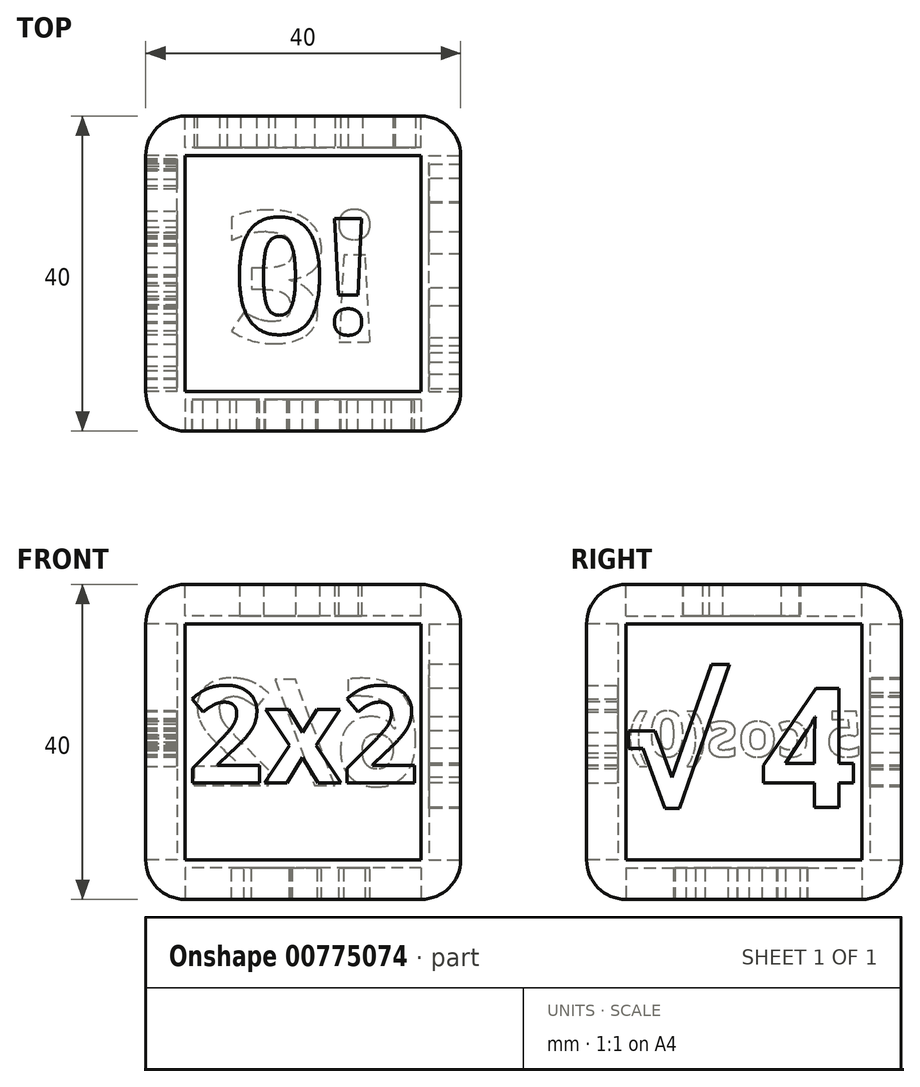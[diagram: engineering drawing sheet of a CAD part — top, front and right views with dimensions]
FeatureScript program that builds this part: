
annotation { "Feature Type Name" : "Feature", "Feature Type Description" : "" }
export const myFeature = defineFeature(function(context is Context, id is Id, definition is map)
    precondition{}
    {
        {
            var Q0;
            Q0=qCreatedBy(makeId("Top.planeOp"),FACE);
            var sketch = newSketch(context, id + "F0", { "sketchPlane" : qUnion([Q0])});
            skLineSegment(sketch, "E0.bottom", {"start": v(20, -20) * mm, "end": v(-20, -20) * mm});
            skLineSegment(sketch, "E0.top", {"start": v(20, 20) * mm, "end": v(-20, 20) * mm});
            skLineSegment(sketch, "E0.left", {"start": v(20, -20) * mm, "end": v(20, 20) * mm});
            skLineSegment(sketch, "E0.right", {"start": v(-20, -20) * mm, "end": v(-20, 20) * mm});
            skPoint(sketch, "E0.middle", {"position": v(0, 0) * mm});
            skSolve(sketch);
        }
        {
            var Q0;
            Q0=makeQuery(id+"F0.imprint","IMPRINT",FACE,{"disambiguationData":[TD([[makeQuery(id+"F0.imprint","IMPRINT",EDGE,{"derivedFrom":sQuery(id+"F0.wireOp",EDGE,"E0.bottom")}),-1.0]])]});
            extrude(context, id + "F1", {"entities" : qUnion([Q0]), "depth" : 40 * mm, "offsetDistance" : 25 * mm});
        }
        {
            var Q0;
            Q0=makeQuery(id+"F1.opExtrude","CAP_FACE",FACE,{"disambiguationData":[OSD([sQuery(id+"F0.wireOp",EDGE,"E0.bottom"),sQuery(id+"F0.wireOp",EDGE,"E0.top"),sQuery(id+"F0.wireOp",EDGE,"E0.left"),sQuery(id+"F0.wireOp",EDGE,"E0.right")])],"isStart":false});
            var Q1;
            Q1=makeQuery(id+"F1.opExtrude","CAP_FACE",FACE,{"disambiguationData":[OSD([sQuery(id+"F0.wireOp",EDGE,"E0.bottom"),sQuery(id+"F0.wireOp",EDGE,"E0.top"),sQuery(id+"F0.wireOp",EDGE,"E0.left"),sQuery(id+"F0.wireOp",EDGE,"E0.right")])],"isStart":true});
            var Q2;
            Q2=makeQuery(id+"F1.opExtrude","SWEPT_FACE",FACE,{"disambiguationData":[OSD([sQuery(id+"F0.wireOp",EDGE,"E0.bottom")])]});
            var Q3;
            Q3=makeQuery(id+"F1.opExtrude","SWEPT_FACE",FACE,{"disambiguationData":[OSD([sQuery(id+"F0.wireOp",EDGE,"E0.top")])]});
            fillet(context, id + "F2", {"entities" : qUnion([Q0, Q1, Q2, Q3]), "radius" : 5 * mm, "tangentPropagation" : true, "allowEdgeOverflow" : false});
        }
        {
            var Q0;
            Q0=makeQuery(id+"F1.opExtrude","CAP_FACE",FACE,{"disambiguationData":[OSD([sQuery(id+"F0.wireOp",EDGE,"E0.bottom"),sQuery(id+"F0.wireOp",EDGE,"E0.top"),sQuery(id+"F0.wireOp",EDGE,"E0.left"),sQuery(id+"F0.wireOp",EDGE,"E0.right")])],"isStart":false});
            extrude(context, id + "F3", {"entities" : qUnion([Q0]), "operationType" : NewBodyOperationType.REMOVE, "oppositeDirection" : true, "depth" : 4 * mm, "offsetDistance" : 25 * mm});
        }
        {
            var Q0;
            Q0=makeQuery(id+"F1.opExtrude","SWEPT_FACE",FACE,{"disambiguationData":[OSD([sQuery(id+"F0.wireOp",EDGE,"E0.top")])]});
            extrude(context, id + "F4", {"entities" : qUnion([Q0]), "operationType" : NewBodyOperationType.REMOVE, "oppositeDirection" : true, "depth" : 4 * mm, "offsetDistance" : 25 * mm});
        }
        {
            var Q0;
            Q0=makeQuery(id+"F1.opExtrude","SWEPT_FACE",FACE,{"disambiguationData":[OSD([sQuery(id+"F0.wireOp",EDGE,"E0.left")])]});
            extrude(context, id + "F5", {"entities" : qUnion([Q0]), "operationType" : NewBodyOperationType.REMOVE, "oppositeDirection" : true, "depth" : 4 * mm, "offsetDistance" : 25 * mm});
        }
        {
            var Q0;
            Q0=makeQuery(id+"F1.opExtrude","SWEPT_FACE",FACE,{"disambiguationData":[OSD([sQuery(id+"F0.wireOp",EDGE,"E0.bottom")])]});
            extrude(context, id + "F6", {"entities" : qUnion([Q0]), "operationType" : NewBodyOperationType.REMOVE, "oppositeDirection" : true, "depth" : 4 * mm, "offsetDistance" : 25 * mm});
        }
        {
            var Q0;
            Q0=makeQuery(id+"F1.opExtrude","SWEPT_FACE",FACE,{"disambiguationData":[OSD([sQuery(id+"F0.wireOp",EDGE,"E0.right")])]});
            extrude(context, id + "F7", {"entities" : qUnion([Q0]), "operationType" : NewBodyOperationType.REMOVE, "oppositeDirection" : true, "depth" : 4 * mm, "offsetDistance" : 25 * mm});
        }
        {
            var Q0;
            Q0=makeQuery(id+"F1.opExtrude","CAP_FACE",FACE,{"disambiguationData":[OSD([sQuery(id+"F0.wireOp",EDGE,"E0.bottom"),sQuery(id+"F0.wireOp",EDGE,"E0.top"),sQuery(id+"F0.wireOp",EDGE,"E0.left"),sQuery(id+"F0.wireOp",EDGE,"E0.right")])],"isStart":true});
            extrude(context, id + "F8", {"entities" : qUnion([Q0]), "operationType" : NewBodyOperationType.REMOVE, "oppositeDirection" : true, "depth" : 4 * mm, "offsetDistance" : 25 * mm});
        }
        {
            var Q0;
            Q0=makeQuery(id+"F3.boolean.opBoolean","COPY",FACE,{"derivedFrom":makeQuery(id+"F3.opExtrude","CAP_FACE",FACE,{"disambiguationData":[OSD([sQuery(id+"F0.wireOp",EDGE,"E0.bottom"),sQuery(id+"F0.wireOp",EDGE,"E0.top"),sQuery(id+"F0.wireOp",EDGE,"E0.left"),sQuery(id+"F0.wireOp",EDGE,"E0.right")])],"isStart":false})});
            var sketch = newSketch(context, id + "F9", { "sketchPlane" : qUnion([Q0])});
            skText(sketch, "E1", { "text": "0!", "fontName": "OpenSans-Bold.ttf"});
            const initialGuessF9  = {"E1": [-0.00883, -0.00758, 1, 0, 0.01467]};
            skSetInitialGuess(sketch, initialGuessF9);
            skSolve(sketch);
        }
        {
            var Q0;
            Q0=makeQuery(id+"F9.imprint","IMPRINT",FACE,{"disambiguationData":[TD([[makeQuery(id+"F9.imprint","IMPRINT",EDGE,{"derivedFrom":sQuery(id+"F9.wireOp",EDGE,"E1.sketch_text.stroke-20")}),-1.0]])]});
            var Q1;
            Q1=makeQuery(id+"F9.imprint","IMPRINT",FACE,{"disambiguationData":[TD([[makeQuery(id+"F9.imprint","IMPRINT",EDGE,{"derivedFrom":sQuery(id+"F9.wireOp",EDGE,"E1.sketch_text.stroke-16")}),-1.0]])]});
            var Q2;
            Q2=makeQuery(id+"F9.imprint","IMPRINT",FACE,{"disambiguationData":[TD([[makeQuery(id+"F9.imprint","IMPRINT",EDGE,{"derivedFrom":sQuery(id+"F9.wireOp",EDGE,"E1.sketch_text.stroke-0")}),-1.0]])]});
            extrude(context, id + "F10", {"entities" : qUnion([Q0, Q1, Q2]), "operationType" : NewBodyOperationType.ADD, "depth" : 4 * mm, "offsetDistance" : 25 * mm});
        }
        {
            var Q0;
            Q0=makeQuery(id+"F5.boolean.opBoolean","COPY",FACE,{"derivedFrom":makeQuery(id+"F5.opExtrude","CAP_FACE",FACE,{"disambiguationData":[OSD([sQuery(id+"F0.wireOp",EDGE,"E0.left")])],"isStart":false})});
            var sketch = newSketch(context, id + "F11", { "sketchPlane" : qUnion([Q0])});
            skText(sketch, "E2", { "text": "√ 4", "fontName": "OpenSans-Bold.ttf"});
            const initialGuessF11  = {"E2": [-0.01505, 0.01168, 1, 0, 0.01527]};
            skSetInitialGuess(sketch, initialGuessF11);
            skSolve(sketch);
        }
        {
            var Q0;
            Q0=makeQuery(id+"F11.imprint","IMPRINT",FACE,{"disambiguationData":[TD([[makeQuery(id+"F11.imprint","IMPRINT",EDGE,{"derivedFrom":sQuery(id+"F11.wireOp",EDGE,"E2.sketch_text.stroke-0")}),-1.0]])]});
            var Q1;
            Q1=makeQuery(id+"F11.imprint","IMPRINT",FACE,{"disambiguationData":[TD([[makeQuery(id+"F11.imprint","IMPRINT",EDGE,{"derivedFrom":sQuery(id+"F11.wireOp",EDGE,"E2.sketch_text.stroke-9")}),-1.0]])]});
            extrude(context, id + "F12", {"entities" : qUnion([Q0, Q1]), "operationType" : NewBodyOperationType.ADD, "depth" : 4 * mm, "offsetDistance" : 25 * mm});
        }
        {
            var Q0;
            Q0=makeQuery(id+"F4.boolean.opBoolean","COPY",FACE,{"derivedFrom":makeQuery(id+"F4.opExtrude","CAP_FACE",FACE,{"disambiguationData":[OSD([sQuery(id+"F0.wireOp",EDGE,"E0.top")])],"isStart":false})});
            var sketch = newSketch(context, id + "F13", { "sketchPlane" : qUnion([Q0])});
            skText(sketch, "E3", { "text": "6/2\n", "fontName": "OpenSans-Bold.ttf"});
            const initialGuessF13  = {"E3": [-0.01494, 0.01446, 1, 0, 0.0136]};
            skSetInitialGuess(sketch, initialGuessF13);
            skSolve(sketch);
        }
        {
            var Q0;
            Q0 = qSketchRegion(id + "F13", true);
            extrude(context, id + "F14", {"entities" : qUnion([Q0]), "operationType" : NewBodyOperationType.ADD, "depth" : 4 * mm, "offsetDistance" : 25 * mm});
        }
        {
            var Q0;
            Q0=makeQuery(id+"F6.boolean.opBoolean","COPY",FACE,{"derivedFrom":makeQuery(id+"F6.opExtrude","CAP_FACE",FACE,{"disambiguationData":[OSD([sQuery(id+"F0.wireOp",EDGE,"E0.bottom")])],"isStart":false})});
            var sketch = newSketch(context, id + "F15", { "sketchPlane" : qUnion([Q0])});
            skText(sketch, "E4", { "text": "2x2", "fontName": "OpenSans-Bold.ttf"});
            const initialGuessF15  = {"E4": [-0.01476, 0.01482, 1, 0, 0.01232]};
            skSetInitialGuess(sketch, initialGuessF15);
            skSolve(sketch);
        }
        {
            var Q0;
            Q0 = qSketchRegion(id + "F15", true);
            extrude(context, id + "F16", {"entities" : qUnion([Q0]), "operationType" : NewBodyOperationType.ADD, "depth" : 4 * mm, "offsetDistance" : 25 * mm});
        }
        {
            var Q0;
            Q0=makeQuery(id+"F7.boolean.opBoolean","COPY",FACE,{"derivedFrom":makeQuery(id+"F7.opExtrude","CAP_FACE",FACE,{"disambiguationData":[OSD([sQuery(id+"F0.wireOp",EDGE,"E0.right")])],"isStart":false})});
            var sketch = newSketch(context, id + "F17", { "sketchPlane" : qUnion([Q0])});
            skText(sketch, "E5", { "text": "5 cos(0)\n", "fontName": "OpenSans-Bold.ttf"});
            const initialGuessF17  = {"E5": [-0.015, 0.01815, 1, 0, 0.00578]};
            skSetInitialGuess(sketch, initialGuessF17);
            skSolve(sketch);
        }
        {
            var Q0;
            Q0 = qSketchRegion(id + "F17", true);
            extrude(context, id + "F18", {"entities" : qUnion([Q0]), "operationType" : NewBodyOperationType.ADD, "depth" : 4 * mm, "offsetDistance" : 25 * mm});
        }
        {
            var Q0;
            Q0=makeQuery(id+"F8.boolean.opBoolean","COPY",FACE,{"derivedFrom":makeQuery(id+"F8.opExtrude","CAP_FACE",FACE,{"disambiguationData":[OSD([sQuery(id+"F0.wireOp",EDGE,"E0.bottom"),sQuery(id+"F0.wireOp",EDGE,"E0.top"),sQuery(id+"F0.wireOp",EDGE,"E0.left"),sQuery(id+"F0.wireOp",EDGE,"E0.right")])],"isStart":false})});
            var sketch = newSketch(context, id + "F19", { "sketchPlane" : qUnion([Q0])});
            skText(sketch, "E6", { "text": "3!", "fontName": "OpenSans-Bold.ttf"});
            const initialGuessF19  = {"E6": [-0.01, -0.00785, 1, 0, 0.01667]};
            skSetInitialGuess(sketch, initialGuessF19);
            skSolve(sketch);
        }
        {
            var Q0;
            Q0 = qSketchRegion(id + "F19", true);
            extrude(context, id + "F20", {"entities" : qUnion([Q0]), "operationType" : NewBodyOperationType.ADD, "depth" : 4 * mm, "offsetDistance" : 25 * mm});
        }
    });
